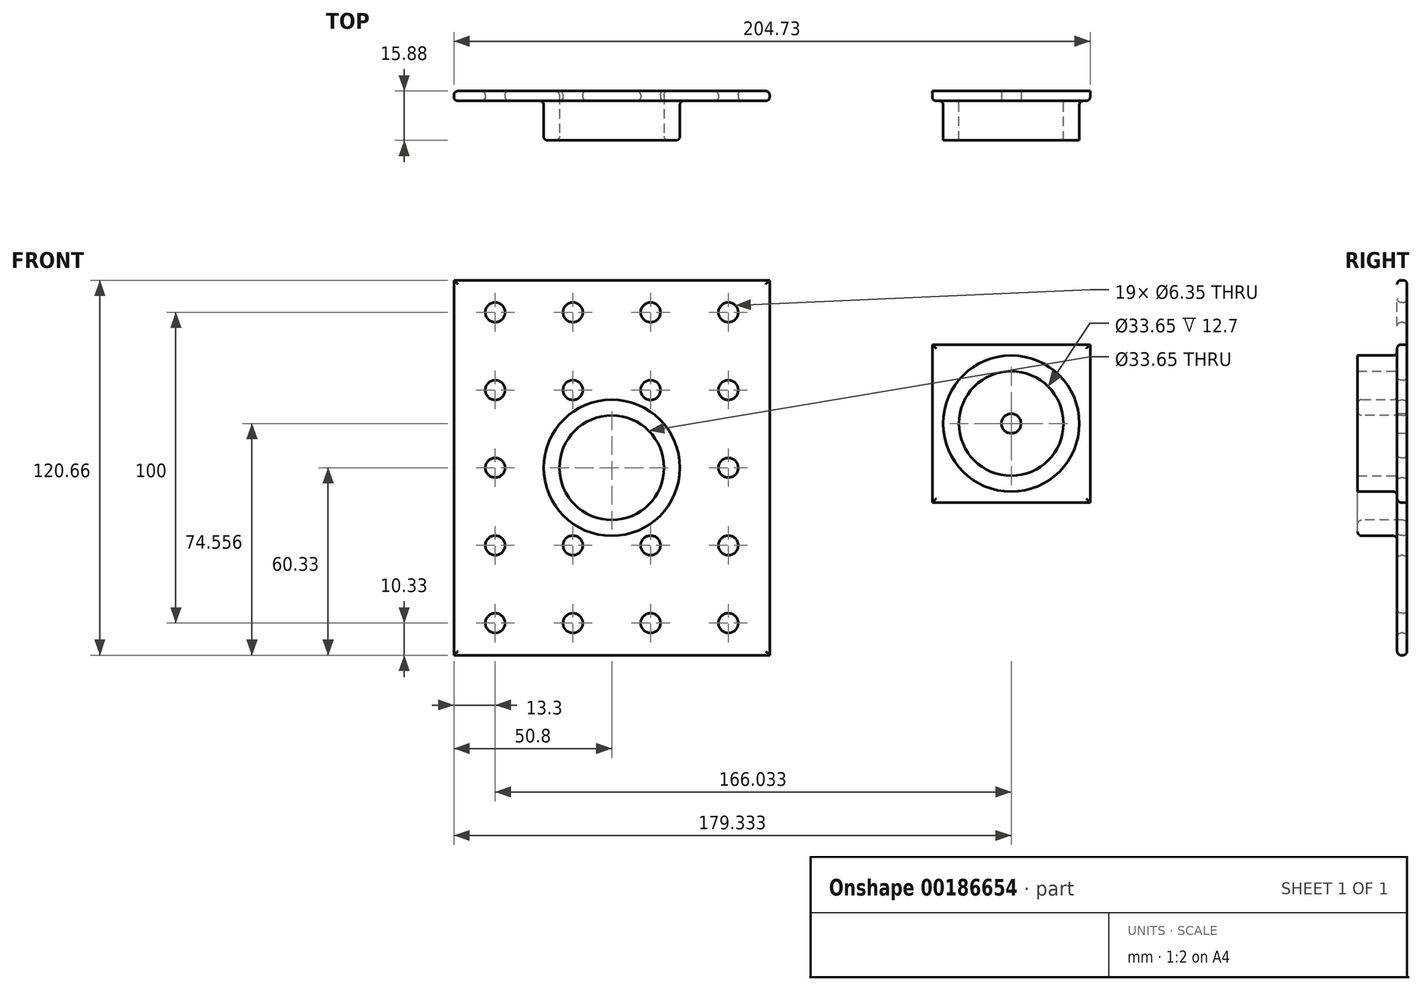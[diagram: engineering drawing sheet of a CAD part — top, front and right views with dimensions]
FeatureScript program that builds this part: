
annotation { "Feature Type Name" : "Feature", "Feature Type Description" : "" }
export const myFeature = defineFeature(function(context is Context, id is Id, definition is map)
    precondition{}
    {
        {
            var Q0;
            Q0=qCreatedBy(makeId("Front.planeOp"),FACE);
            var sketch = newSketch(context, id + "F0", { "sketchPlane" : qUnion([Q0])});
            skLineSegment(sketch, "E0.bottom", {"start": v(-50.8, 60.33) * mm, "end": v(50.8, 60.33) * mm});
            skLineSegment(sketch, "E0.top", {"start": v(-50.8, -60.33) * mm, "end": v(50.8, -60.33) * mm});
            skLineSegment(sketch, "E0.left", {"start": v(-50.8, 60.33) * mm, "end": v(-50.8, -60.33) * mm});
            skLineSegment(sketch, "E0.right", {"start": v(50.8, 60.33) * mm, "end": v(50.8, -60.33) * mm});
            skPoint(sketch, "E0.middle", {"position": v(0, 0) * mm});
            skLineSegment(sketch, "E1", {"start": v(-12.5, 0) * mm, "end": v(12.5, 0) * mm, "construction": true});
            skLineSegment(sketch, "E2", {"start": v(12.5, 0) * mm, "end": v(37.5, 0) * mm, "construction": true});
            skLineSegment(sketch, "E3", {"start": v(37.5, 0) * mm, "end": v(37.5, -25) * mm, "construction": true});
            skLineSegment(sketch, "E4", {"start": v(37.5, -25) * mm, "end": v(12.5, -25) * mm, "construction": true});
            skLineSegment(sketch, "E5", {"start": v(12.5, -25) * mm, "end": v(-12.5, -25) * mm, "construction": true});
            skLineSegment(sketch, "E6", {"start": v(37.5, 0) * mm, "end": v(37.5, 25) * mm, "construction": true});
            skLineSegment(sketch, "E7", {"start": v(37.5, 25) * mm, "end": v(12.5, 25) * mm, "construction": true});
            skLineSegment(sketch, "E8", {"start": v(12.5, 25) * mm, "end": v(-12.5, 25) * mm, "construction": true});
            skLineSegment(sketch, "E9", {"start": v(-12.5, 25) * mm, "end": v(-37.5, 25) * mm, "construction": true});
            skLineSegment(sketch, "E10", {"start": v(-12.5, 0) * mm, "end": v(-37.5, 0) * mm, "construction": true});
            skLineSegment(sketch, "E11", {"start": v(-12.5, -25) * mm, "end": v(-37.5, -25) * mm, "construction": true});
            skLineSegment(sketch, "E12", {"start": v(37.5, 25) * mm, "end": v(37.5, 50) * mm, "construction": true});
            skLineSegment(sketch, "E13", {"start": v(37.5, 50) * mm, "end": v(12.5, 50) * mm, "construction": true});
            skLineSegment(sketch, "E14", {"start": v(12.5, 50) * mm, "end": v(-12.5, 50) * mm, "construction": true});
            skLineSegment(sketch, "E15", {"start": v(-12.5, 50) * mm, "end": v(-37.5, 50) * mm, "construction": true});
            skLineSegment(sketch, "E16", {"start": v(37.5, -25) * mm, "end": v(37.5, -50) * mm, "construction": true});
            skLineSegment(sketch, "E17", {"start": v(37.5, -50) * mm, "end": v(12.5, -50) * mm, "construction": true});
            skLineSegment(sketch, "E18", {"start": v(12.5, -50) * mm, "end": v(-12.5, -50) * mm, "construction": true});
            skLineSegment(sketch, "E19", {"start": v(-12.5, -50) * mm, "end": v(-37.5, -50) * mm, "construction": true});
            skCircle(sketch, "E20", {"center": v(-37.5, 50) * mm, "radius": 3.18 * mm});
            skCircle(sketch, "E21", {"center": v(12.5, -25) * mm, "radius": 3.18 * mm});
            skCircle(sketch, "E22", {"center": v(37.5, -25) * mm, "radius": 3.18 * mm});
            skCircle(sketch, "E23", {"center": v(-12.5, -25) * mm, "radius": 3.18 * mm});
            skCircle(sketch, "E24", {"center": v(-12.5, -50) * mm, "radius": 3.18 * mm});
            skCircle(sketch, "E25", {"center": v(12.5, -50) * mm, "radius": 3.18 * mm});
            skCircle(sketch, "E26", {"center": v(37.5, -50) * mm, "radius": 3.18 * mm});
            skCircle(sketch, "E27", {"center": v(-12.5, 50) * mm, "radius": 3.18 * mm});
            skCircle(sketch, "E28", {"center": v(12.5, 50) * mm, "radius": 3.18 * mm});
            skCircle(sketch, "E29", {"center": v(37.5, 50) * mm, "radius": 3.18 * mm});
            skCircle(sketch, "E30", {"center": v(-37.5, -50) * mm, "radius": 3.18 * mm});
            skCircle(sketch, "E31", {"center": v(-37.5, -25) * mm, "radius": 3.18 * mm});
            skCircle(sketch, "E32", {"center": v(-37.5, 0) * mm, "radius": 3.18 * mm});
            skCircle(sketch, "E33", {"center": v(-37.5, 25) * mm, "radius": 3.18 * mm});
            skCircle(sketch, "E34", {"center": v(-12.5, 25) * mm, "radius": 3.18 * mm});
            skCircle(sketch, "E35", {"center": v(12.5, 25) * mm, "radius": 3.18 * mm});
            skCircle(sketch, "E36", {"center": v(0, 0) * mm, "radius": 16.83 * mm});
            skCircle(sketch, "E37", {"center": v(37.5, 0) * mm, "radius": 3.18 * mm});
            skCircle(sketch, "E38", {"center": v(37.5, 25) * mm, "radius": 3.18 * mm});
            skCircle(sketch, "E39.0", {"center": v(0, 0) * mm, "radius": 21.9 * mm});
            skSolve(sketch);
        }
        {
            var Q0;
            Q0=makeQuery(id+"F0.imprint","IMPRINT",FACE,{"disambiguationData":[TD([[makeQuery(id+"F0.imprint","IMPRINT",EDGE,{"derivedFrom":sQuery(id+"F0.wireOp",EDGE,"E0.bottom")}),-1.0]])]});
            var Q1;
            Q1=makeQuery(id+"F0.imprint","IMPRINT",FACE,{"disambiguationData":[TD([[makeQuery(id+"F0.imprint","IMPRINT",EDGE,{"derivedFrom":sQuery(id+"F0.wireOp",EDGE,"E36")}),-1.0]])]});
            extrude(context, id + "F1", {"entities" : qUnion([Q0, Q1]), "oppositeDirection" : true, "depth" : 3.17 * mm});
        }
        {
            var Q0;
            Q0=makeQuery(id+"F0.imprint","IMPRINT",FACE,{"disambiguationData":[TD([[makeQuery(id+"F0.imprint","IMPRINT",EDGE,{"derivedFrom":sQuery(id+"F0.wireOp",EDGE,"E36")}),-1.0]])]});
            extrude(context, id + "F2", {"entities" : qUnion([Q0]), "operationType" : NewBodyOperationType.ADD, "depth" : 12.7 * mm});
        }
        {
            var Q0;
            Q0=makeQuery(id+"F2.opExtrude","CAP_EDGE",EDGE,{"disambiguationData":[OSD([sQuery(id+"F0.wireOp",EDGE,"E36")])],"isStart":false});
            var Q1;
            Q1=makeQuery(id+"F2.opExtrude","CAP_EDGE",EDGE,{"disambiguationData":[OSD([sQuery(id+"F0.wireOp",EDGE,"E39.0")])],"isStart":false});
            var Q2;
            Q2=makeQuery(id+"F2.opExtrude","CAP_EDGE",EDGE,{"disambiguationData":[OSD([sQuery(id+"F0.wireOp",EDGE,"E39.0")])],"isStart":true});
            var Q3;
            Q3=makeQuery(id+"F1.opExtrude","CAP_FACE",FACE,{"disambiguationData":[OSD([sQuery(id+"F0.wireOp",EDGE,"E0.bottom"),sQuery(id+"F0.wireOp",EDGE,"E0.top"),sQuery(id+"F0.wireOp",EDGE,"E0.left"),sQuery(id+"F0.wireOp",EDGE,"E0.right"),sQuery(id+"F0.wireOp",EDGE,"E20"),sQuery(id+"F0.wireOp",EDGE,"E21"),sQuery(id+"F0.wireOp",EDGE,"E22"),sQuery(id+"F0.wireOp",EDGE,"E23"),sQuery(id+"F0.wireOp",EDGE,"E24"),sQuery(id+"F0.wireOp",EDGE,"E25"),sQuery(id+"F0.wireOp",EDGE,"E26"),sQuery(id+"F0.wireOp",EDGE,"E27"),sQuery(id+"F0.wireOp",EDGE,"E28"),sQuery(id+"F0.wireOp",EDGE,"E29"),sQuery(id+"F0.wireOp",EDGE,"E30"),sQuery(id+"F0.wireOp",EDGE,"E31"),sQuery(id+"F0.wireOp",EDGE,"E32"),sQuery(id+"F0.wireOp",EDGE,"E33"),sQuery(id+"F0.wireOp",EDGE,"E34"),sQuery(id+"F0.wireOp",EDGE,"E35"),sQuery(id+"F0.wireOp",EDGE,"E36"),sQuery(id+"F0.wireOp",EDGE,"E37"),sQuery(id+"F0.wireOp",EDGE,"E38")])],"isStart":true});
            var Q4;
            Q4=makeQuery(id+"F1.opExtrude","CAP_FACE",FACE,{"disambiguationData":[OSD([sQuery(id+"F0.wireOp",EDGE,"E0.bottom"),sQuery(id+"F0.wireOp",EDGE,"E0.top"),sQuery(id+"F0.wireOp",EDGE,"E0.left"),sQuery(id+"F0.wireOp",EDGE,"E0.right"),sQuery(id+"F0.wireOp",EDGE,"E20"),sQuery(id+"F0.wireOp",EDGE,"E21"),sQuery(id+"F0.wireOp",EDGE,"E22"),sQuery(id+"F0.wireOp",EDGE,"E23"),sQuery(id+"F0.wireOp",EDGE,"E24"),sQuery(id+"F0.wireOp",EDGE,"E25"),sQuery(id+"F0.wireOp",EDGE,"E26"),sQuery(id+"F0.wireOp",EDGE,"E27"),sQuery(id+"F0.wireOp",EDGE,"E28"),sQuery(id+"F0.wireOp",EDGE,"E29"),sQuery(id+"F0.wireOp",EDGE,"E30"),sQuery(id+"F0.wireOp",EDGE,"E31"),sQuery(id+"F0.wireOp",EDGE,"E32"),sQuery(id+"F0.wireOp",EDGE,"E33"),sQuery(id+"F0.wireOp",EDGE,"E34"),sQuery(id+"F0.wireOp",EDGE,"E35"),sQuery(id+"F0.wireOp",EDGE,"E36"),sQuery(id+"F0.wireOp",EDGE,"E37"),sQuery(id+"F0.wireOp",EDGE,"E38")])],"isStart":false});
            fillet(context, id + "F3", {"entities" : qUnion([Q0, Q1, Q2, Q3, Q4]), "radius" : 1.27 * mm, "tangentPropagation" : true, "allowEdgeOverflow" : false});
        }
        {
            var Q0;
            Q0=qCreatedBy(makeId("Front.planeOp"),FACE);
            var sketch = newSketch(context, id + "F4", { "sketchPlane" : qUnion([Q0])});
            skLineSegment(sketch, "E40.bottom", {"start": v(103.13, 39.63) * mm, "end": v(153.93, 39.63) * mm});
            skLineSegment(sketch, "E40.top", {"start": v(103.13, -11.17) * mm, "end": v(153.93, -11.17) * mm});
            skLineSegment(sketch, "E40.left", {"start": v(103.13, 39.63) * mm, "end": v(103.13, -11.17) * mm});
            skLineSegment(sketch, "E40.right", {"start": v(153.93, 39.63) * mm, "end": v(153.93, -11.17) * mm});
            skPoint(sketch, "E40.middle", {"position": v(128.53, 14.23) * mm});
            skCircle(sketch, "E41", {"center": v(128.53, 14.23) * mm, "radius": 16.83 * mm});
            skCircle(sketch, "E42", {"center": v(128.53, 14.23) * mm, "radius": 21.9 * mm});
            skCircle(sketch, "E43", {"center": v(128.53, 14.23) * mm, "radius": 3.18 * mm});
            skSolve(sketch);
        }
        {
            var Q0;
            Q0=makeQuery(id+"F4.imprint","IMPRINT",FACE,{"disambiguationData":[TD([[makeQuery(id+"F4.imprint","IMPRINT",EDGE,{"derivedFrom":sQuery(id+"F4.wireOp",EDGE,"E40.bottom")}),-1.0]])]});
            var Q1;
            Q1=makeQuery(id+"F4.imprint","IMPRINT",FACE,{"disambiguationData":[TD([[makeQuery(id+"F4.imprint","IMPRINT",EDGE,{"derivedFrom":sQuery(id+"F4.wireOp",EDGE,"E41")}),-1.0]])]});
            var Q2;
            Q2=makeQuery(id+"F4.imprint","IMPRINT",FACE,{"disambiguationData":[TD([[makeQuery(id+"F4.imprint","IMPRINT",EDGE,{"derivedFrom":sQuery(id+"F4.wireOp",EDGE,"E41")}),1.0]])]});
            var Q3;
            Q3=makeQuery(id+"F1.opExtrude","CAP_FACE",FACE,{"disambiguationData":[OSD([sQuery(id+"F0.wireOp",EDGE,"E0.bottom"),sQuery(id+"F0.wireOp",EDGE,"E0.top"),sQuery(id+"F0.wireOp",EDGE,"E0.left"),sQuery(id+"F0.wireOp",EDGE,"E0.right"),sQuery(id+"F0.wireOp",EDGE,"E20"),sQuery(id+"F0.wireOp",EDGE,"E21"),sQuery(id+"F0.wireOp",EDGE,"E22"),sQuery(id+"F0.wireOp",EDGE,"E23"),sQuery(id+"F0.wireOp",EDGE,"E24"),sQuery(id+"F0.wireOp",EDGE,"E25"),sQuery(id+"F0.wireOp",EDGE,"E26"),sQuery(id+"F0.wireOp",EDGE,"E27"),sQuery(id+"F0.wireOp",EDGE,"E28"),sQuery(id+"F0.wireOp",EDGE,"E29"),sQuery(id+"F0.wireOp",EDGE,"E30"),sQuery(id+"F0.wireOp",EDGE,"E31"),sQuery(id+"F0.wireOp",EDGE,"E32"),sQuery(id+"F0.wireOp",EDGE,"E33"),sQuery(id+"F0.wireOp",EDGE,"E34"),sQuery(id+"F0.wireOp",EDGE,"E35"),sQuery(id+"F0.wireOp",EDGE,"E36"),sQuery(id+"F0.wireOp",EDGE,"E37"),sQuery(id+"F0.wireOp",EDGE,"E38")])],"isStart":false});
            extrude(context, id + "F5", {"entities" : qUnion([Q0, Q1, Q2]), "endBound" : BoundingType.UP_TO_SURFACE, "oppositeDirection" : true, "endBoundEntityFace" : qUnion([Q3]), "depth" : 25.4 * mm});
        }
        {
            var Q0;
            Q0=makeQuery(id+"F4.imprint","IMPRINT",FACE,{"disambiguationData":[TD([[makeQuery(id+"F4.imprint","IMPRINT",EDGE,{"derivedFrom":sQuery(id+"F4.wireOp",EDGE,"E41")}),-1.0]])]});
            var Q1;
            Q1=makeQuery(id+"F2.opExtrude","CAP_FACE",FACE,{"disambiguationData":[OSD([sQuery(id+"F0.wireOp",EDGE,"E36"),sQuery(id+"F0.wireOp",EDGE,"E39.0")])],"isStart":false});
            extrude(context, id + "F6", {"entities" : qUnion([Q0]), "operationType" : NewBodyOperationType.ADD, "endBound" : BoundingType.UP_TO_SURFACE, "endBoundEntityFace" : qUnion([Q1]), "depth" : 25.4 * mm});
        }
        {
            var Q0;
            Q0=makeQuery(id+"F6.opExtrude","TWEAK_EDGE",EDGE,{"derivedFrom":[makeQuery(id+"F2.opExtrude","CAP_FACE",FACE,{"disambiguationData":[OSD([sQuery(id+"F0.wireOp",EDGE,"E36"),sQuery(id+"F0.wireOp",EDGE,"E39.0")])],"isStart":false}),makeQuery(id+"F4.imprint","IMPRINT",EDGE,{"derivedFrom":sQuery(id+"F4.wireOp",EDGE,"E41")})]});
            var Q1;
            Q1=makeQuery(id+"F6.opExtrude","TWEAK_EDGE",EDGE,{"derivedFrom":[makeQuery(id+"F2.opExtrude","CAP_FACE",FACE,{"disambiguationData":[OSD([sQuery(id+"F0.wireOp",EDGE,"E36"),sQuery(id+"F0.wireOp",EDGE,"E39.0")])],"isStart":false}),makeQuery(id+"F4.imprint","IMPRINT",EDGE,{"derivedFrom":sQuery(id+"F4.wireOp",EDGE,"E42")})]});
            var Q2;
            {var subQ0=sQuery(id+"F4.wireOp",EDGE,"E40.top");var subQ1=sQuery(id+"F4.wireOp",EDGE,"E40.right");var subQ2=sQuery(id+"F4.wireOp",EDGE,"E40.left");var subQ3=sQuery(id+"F4.wireOp",EDGE,"E40.bottom");Q2=makeQuery(id+"F6.boolean.opBoolean","SPLIT",FACE,{"disambiguationData":[TD([makeQuery(id+"F5.opExtrude","SWEPT_FACE",FACE,{"disambiguationData":[OSD([subQ3])]})])],"derivedFrom":makeQuery(id+"F5.opExtrude","CAP_FACE",FACE,{"disambiguationData":[OSD([subQ3,subQ0,subQ2,subQ1,sQuery(id+"F4.wireOp",EDGE,"E43")])],"isStart":true})});}
            var Q3;
            Q3=makeQuery(id+"F5.opExtrude","CAP_FACE",FACE,{"disambiguationData":[OSD([sQuery(id+"F0.wireOp",EDGE,"E0.bottom"),sQuery(id+"F0.wireOp",EDGE,"E0.top"),sQuery(id+"F0.wireOp",EDGE,"E0.left"),sQuery(id+"F0.wireOp",EDGE,"E0.right"),sQuery(id+"F0.wireOp",EDGE,"E20"),sQuery(id+"F0.wireOp",EDGE,"E21"),sQuery(id+"F0.wireOp",EDGE,"E22"),sQuery(id+"F0.wireOp",EDGE,"E23"),sQuery(id+"F0.wireOp",EDGE,"E24"),sQuery(id+"F0.wireOp",EDGE,"E25"),sQuery(id+"F0.wireOp",EDGE,"E26"),sQuery(id+"F0.wireOp",EDGE,"E27"),sQuery(id+"F0.wireOp",EDGE,"E28"),sQuery(id+"F0.wireOp",EDGE,"E29"),sQuery(id+"F0.wireOp",EDGE,"E30"),sQuery(id+"F0.wireOp",EDGE,"E31"),sQuery(id+"F0.wireOp",EDGE,"E32"),sQuery(id+"F0.wireOp",EDGE,"E33"),sQuery(id+"F0.wireOp",EDGE,"E34"),sQuery(id+"F0.wireOp",EDGE,"E35"),sQuery(id+"F0.wireOp",EDGE,"E36"),sQuery(id+"F0.wireOp",EDGE,"E37"),sQuery(id+"F0.wireOp",EDGE,"E38")])],"isStart":false});
            fillet(context, id + "F7", {"entities" : qUnion([Q0, Q1, Q2, Q3]), "radius" : 1.27 * mm, "tangentPropagation" : true, "allowEdgeOverflow" : false});
        }
    });
